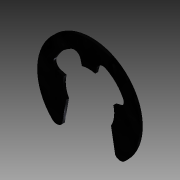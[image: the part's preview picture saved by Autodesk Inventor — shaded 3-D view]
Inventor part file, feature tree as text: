
AUTODESK INVENTOR PART (.ipt)
format: ipt  version: 2014 (Build 180170000, 170)  size: 100,864 bytes
history: native  units: in
note: dims shown in document units (in); Inventor stores cm internally (conversion verified against a paired STEP export)
features: extrude x1, sketch x1
ambient origin geometry x8: Origin, YZ Plane, XZ Plane, XY Plane, X Axis, Y Axis, Z Axis, Center Point
bodies: Solid1 (feature_tree)
feature tree (2):
  extrude  "Extrusion1"  Depth=0.445in
  sketch  "Sketch1"  dims[d0=0.89in d2=0.445in d3=0.05in d4=0.0in]
